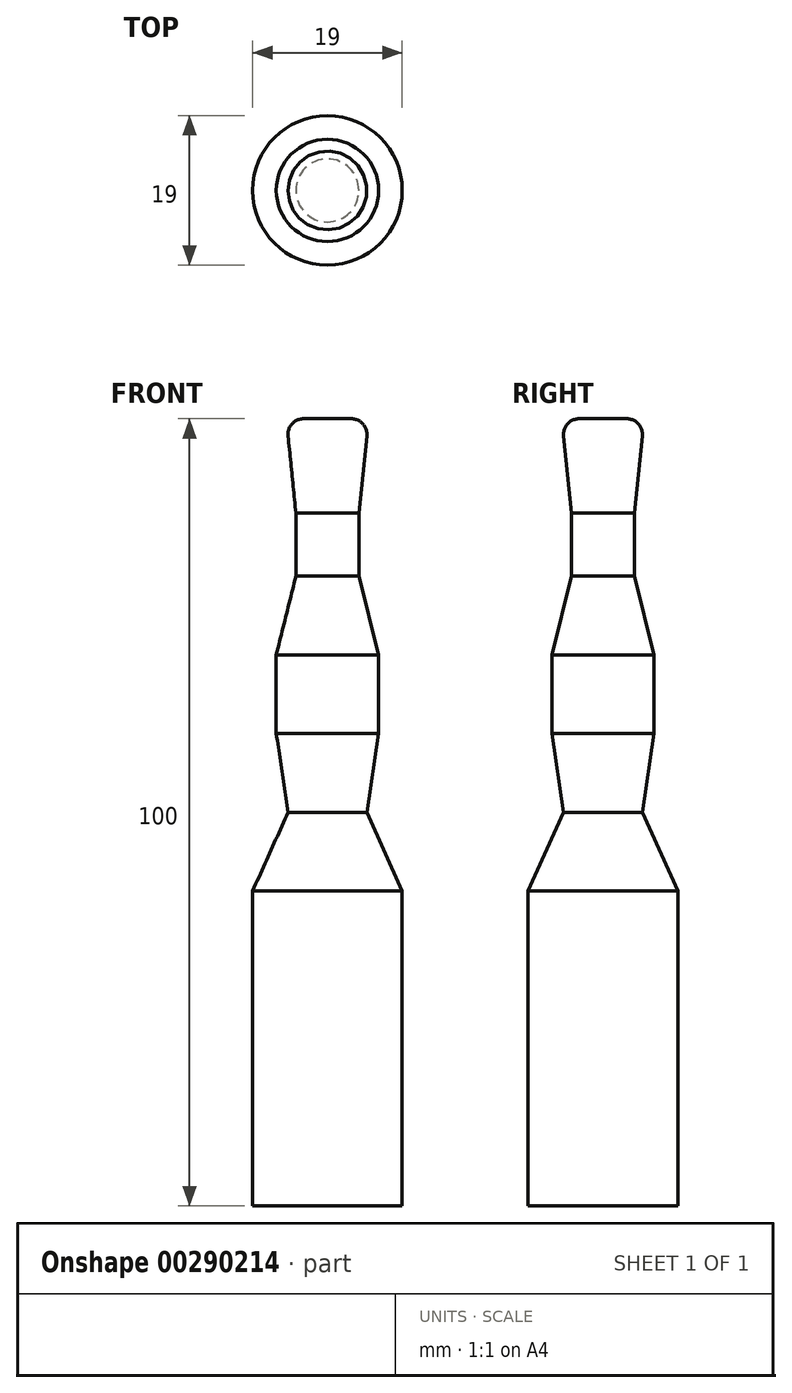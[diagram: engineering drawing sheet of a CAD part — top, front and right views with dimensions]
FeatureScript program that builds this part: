
annotation { "Feature Type Name" : "Feature", "Feature Type Description" : "" }
export const myFeature = defineFeature(function(context is Context, id is Id, definition is map)
    precondition{}
    {
        {
            var Q0;
            Q0=qCreatedBy(makeId("Front.planeOp"),FACE);
            var sketch = newSketch(context, id + "F0", { "sketchPlane" : qUnion([Q0])});
            skLineSegment(sketch, "E0", {"start": v(0, 0) * mm, "end": v(0, 0) * mm});
            skArc(sketch, "E1", {"start": v(0, -0.01) * mm, "mid": v(0, 0) * mm, "end": v(0, 0) * mm});
            skLineSegment(sketch, "E2", {"start": v(0, -0.01) * mm, "end": v(0, -0.01) * mm});
            skLineSegment(sketch, "E3", {"start": v(0.03, -81.66) * mm, "end": v(0, -81.66) * mm});
            skLineSegment(sketch, "E4", {"start": v(0, 0) * mm, "end": v(3.01, 0) * mm});
            skArc(sketch, "E5", {"start": v(5, -2.2) * mm, "mid": v(4.5, -0.66) * mm, "end": v(3.01, 0) * mm});
            skLineSegment(sketch, "E6", {"start": v(5, -2.2) * mm, "end": v(4, -12) * mm});
            skLineSegment(sketch, "E7", {"start": v(4, -12) * mm, "end": v(4, -20) * mm});
            skLineSegment(sketch, "E8", {"start": v(4, -20) * mm, "end": v(6.5, -30) * mm});
            skLineSegment(sketch, "E9", {"start": v(6.5, -30) * mm, "end": v(6.5, -40) * mm});
            skLineSegment(sketch, "E10", {"start": v(6.5, -40) * mm, "end": v(5, -50) * mm});
            skLineSegment(sketch, "E11", {"start": v(5, -50) * mm, "end": v(9.5, -60) * mm});
            skLineSegment(sketch, "E12", {"start": v(9.5, -60) * mm, "end": v(9.5, -100) * mm});
            skLineSegment(sketch, "E13", {"start": v(9.5, -100) * mm, "end": v(0, -100) * mm});
            skLineSegment(sketch, "E14", {"start": v(0, -100) * mm, "end": v(0, 0) * mm});
            skSolve(sketch);
        }
        {
            var Q0;
            {var subQ0=sQuery(id+"F0.wireOp",EDGE,"E14");var subQ1=sQuery(id+"F0.wireOp",EDGE,"E1");var subQ3=makeQuery(id+"F0.imprint","INTERSECT",VERTEX,{"derivedFrom":[subQ1,subQ0]});Q0=makeQuery(id+"F0.imprint","IMPRINT",FACE,{"disambiguationData":[TD([[makeQuery(id+"F0.imprint","IMPRINT",EDGE,{"disambiguationData":[TD([[subQ3,-1.0]])],"derivedFrom":subQ1}),1.0]])]});}
            var Q1;
            {var subQ1=sQuery(id+"F0.wireOp",EDGE,"E4");Q1=makeQuery(id+"F0.imprint","IMPRINT",FACE,{"disambiguationData":[TD([[makeQuery(id+"F0.imprint","IMPRINT",EDGE,{"derivedFrom":subQ1}),-1.0]])]});}
            var Q2;
            Q2=sQuery(id+"F0.wireOp",EDGE,"E14");
            revolve(context, id + "F1", {"entities" : qUnion([Q0, Q1]), "axis" : qUnion([Q2]), "revolveType" : RevolveType.FULL});
        }
    });
